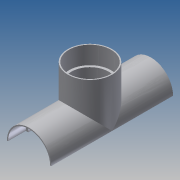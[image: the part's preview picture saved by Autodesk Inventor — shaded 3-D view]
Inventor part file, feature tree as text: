
AUTODESK INVENTOR PART (.ipt)
format: ipt  version: 2014 SP1 (Build 180222100, 222)  size: 228,352 bytes
history: native  units: in
note: dims shown in document units (in); Inventor stores cm internally (conversion verified against a paired STEP export)
features: sketch x15, extrude x11, plane x4
ambient origin geometry x8: Origin, YZ Plane, XZ Plane, XY Plane, X Axis, Y Axis, Z Axis, Center Point
bodies: Solid1 (feature_tree)
feature tree (30):
  extrude  "mainBody"  Depth=6.875in TaperAngle=0.0deg
  sketch  "Sketch10"  dims[d29=3.4375in d30=2.5in]
  plane  "Work Plane5"
  extrude  "TBody"  Depth=3.4375in
  extrude  "TSocket"  Depth=2.375in
  extrude  "TTube"  Depth=2.1in
  extrude  "mainTube"  Depth=2.1in
  extrude  "mainSocket1"  Depth=2.375in
  extrude  "mainSocket2"  Depth=2.375in
  extrude  "Extrusion18"  Depth=8.0in TaperAngle=0.0deg
  sketch  "Sketch23"  dims[d85=0.0258in d86=0.5in]
  plane  "Work Plane9"
  extrude  "15deg"  Depth=0.1in TaperAngle=0.0deg
  sketch  "Sketch28"
  plane  "Work Plane12"
  extrude  "Extrusion23"  Depth=0.5in
  sketch  "Sketch30"
  plane  "Work Plane13"
  extrude  "Extrusion24"  Depth=0.1in TaperAngle=0.0deg
  sketch  "Sketch1"  dims[d0=2.5in d1=6.875in d2=0.0in]
  sketch  "Sketch11"  dims[d31=1.5in d32=1.25in d33=0.0in d34=0.0in d35=2.375in]
  sketch  "Sketch12"  dims[d37=1.0in d38=0.0in d39=2.1in]
  sketch  "Sketch13"  dims[d41=1.5in d42=0.0in d43=2.1in]
  sketch  "Sketch14"  dims[d45=7.0in d46=0.0in d47=2.375in]
  sketch  "Sketch15"  dims[d49=1.0in d50=0.0in d51=2.375in]
  sketch  "Sketch16"  dims[d53=1.0in d54=0.0in d66=8.0in d67=0.0in]
  sketch  "Sketch21"  dims[d75=-0.1021in d76=0.1in d77=0.0in]
  sketch  "Sketch24"  dims[d87=0.25in d88=0.0in d89=0.1in d90=0.0in]
  sketch  "Sketch29"
  sketch  "Sketch33"
